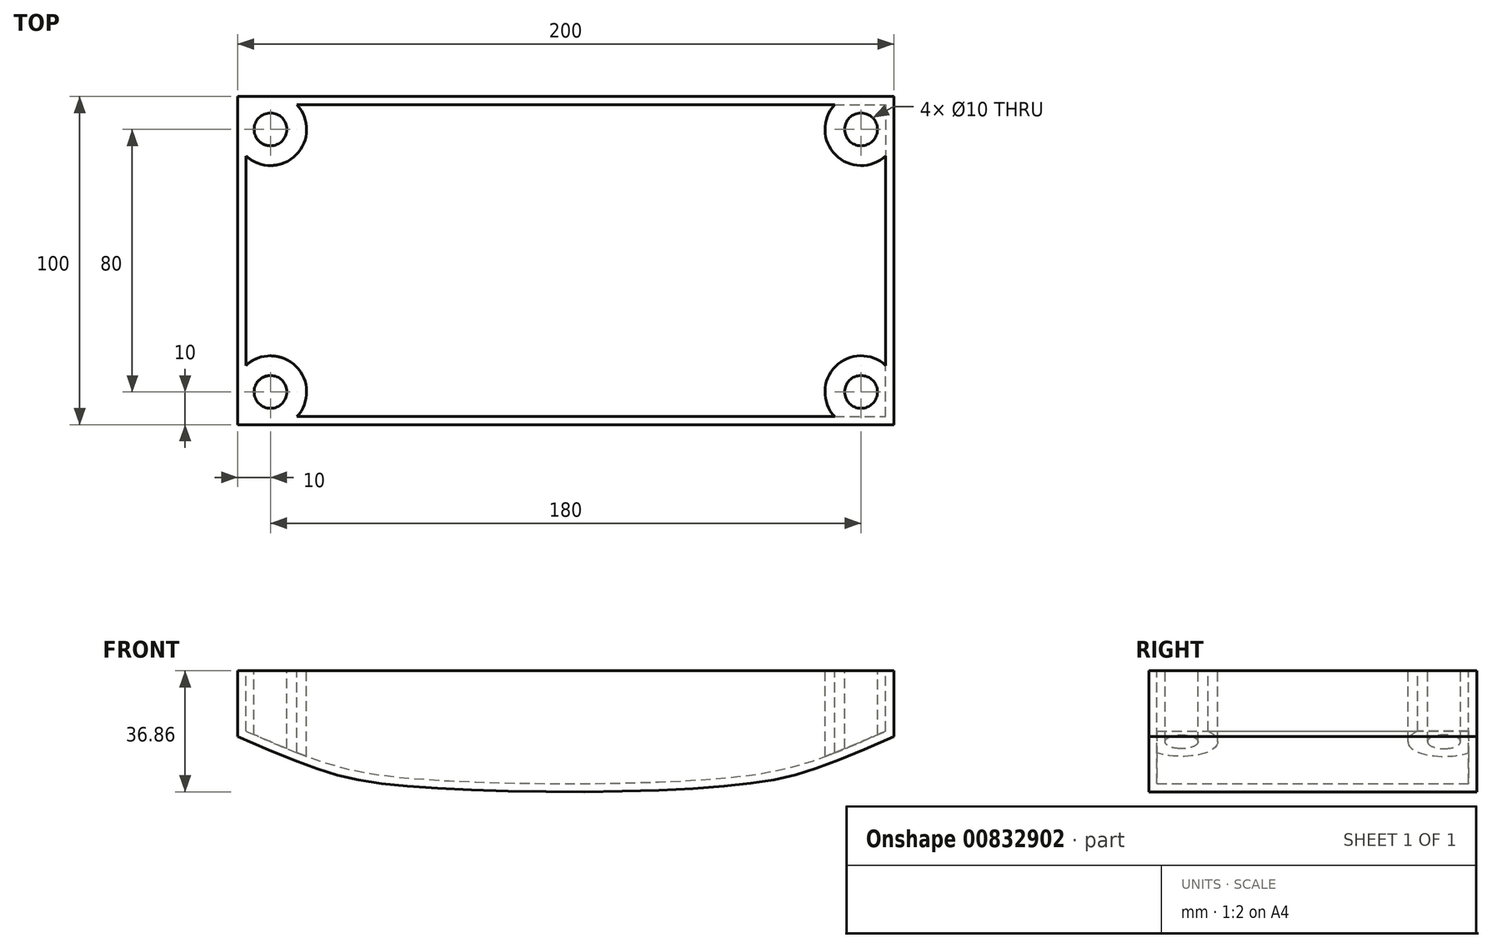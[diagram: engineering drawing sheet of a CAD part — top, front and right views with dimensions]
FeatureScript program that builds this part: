
annotation { "Feature Type Name" : "Feature", "Feature Type Description" : "" }
export const myFeature = defineFeature(function(context is Context, id is Id, definition is map)
    precondition{}
    {
        {
            var Q0;
            Q0=qCreatedBy(makeId("Front.planeOp"),FACE);
            var sketch = newSketch(context, id + "F0", { "sketchPlane" : qUnion([Q0])});
            skLineSegment(sketch, "E0.bottom", {"start": v(-100, 20) * mm, "end": v(100, 20) * mm});
            skLineSegment(sketch, "E0.left", {"start": v(-100, 20) * mm, "end": v(-100, 0) * mm});
            skLineSegment(sketch, "E0.right", {"start": v(100, 20) * mm, "end": v(100, 0) * mm});
            skFitSpline(sketch, "E1", {"points": [v(-100, 0) * mm, v(-50, -15) * mm, v(50, -15) * mm, v(100, 0) * mm], "startDerivative": vector(237.19, -104) * mm, "endDerivative": vector(226.22, 101.3) * mm});
            skPoint(sketch, "E2.orphan", {"position": v(100, -20) * mm});
            skSolve(sketch);
        }
        {
            var Q0;
            Q0=makeQuery(id+"F0.imprint","IMPRINT",FACE,{"disambiguationData":[TD([[makeQuery(id+"F0.imprint","IMPRINT",EDGE,{"derivedFrom":sQuery(id+"F0.wireOp",EDGE,"E0.bottom")}),-1.0]])]});
            extrude(context, id + "F1", {"entities" : qUnion([Q0]), "endBound" : BoundingType.SYMMETRIC, "depth" : 100 * mm, "offsetDistance" : 25 * mm});
        }
        {
            var Q0;
            Q0=makeQuery(id+"F1.opExtrude","SWEPT_FACE",FACE,{"disambiguationData":[OSD([sQuery(id+"F0.wireOp",EDGE,"E0.bottom")])]});
            shell(context, id + "F2", {"entities" : qUnion([Q0]), "thickness" : 2.5 * mm});
        }
        {
            var Q0;
            Q0=makeQuery(id+"F1.opExtrude","SWEPT_FACE",FACE,{"disambiguationData":[OSD([sQuery(id+"F0.wireOp",EDGE,"E0.bottom")])]});
            var sketch = newSketch(context, id + "F3", { "sketchPlane" : qUnion([Q0])});
            skCircle(sketch, "E3", {"center": v(-90, -40) * mm, "radius": 5 * mm});
            skCircle(sketch, "E4", {"center": v(-90, -40) * mm, "radius": 11 * mm});
            skSolve(sketch);
        }
        {
            var Q0;
            Q0=makeQuery(id+"F3.imprint","IMPRINT",FACE,{"disambiguationData":[TD([[makeQuery(id+"F3.imprint","IMPRINT",EDGE,{"derivedFrom":sQuery(id+"F3.wireOp",EDGE,"E3")}),-1.0]])]});
            extrude(context, id + "F4", {"entities" : qUnion([Q0]), "endBound" : BoundingType.UP_TO_NEXT, "oppositeDirection" : true, "depth" : 25 * mm, "offsetDistance" : 25 * mm});
        }
        {
            var Q0;
            Q0=makeQuery(id+"F4.opExtrude","SWEPT_BODY",BODY,{"disambiguationData":[OSD([sQuery(id+"F0.wireOp",EDGE,"E0.bottom"),sQuery(id+"F0.wireOp",EDGE,"E0.left"),sQuery(id+"F3.wireOp",EDGE,"E3"),sQuery(id+"F3.wireOp",EDGE,"E4")])]});
            var Q1;
            Q1=qCreatedBy(makeId("Front.planeOp"),FACE);
            mirror(context, id + "F5", {"entities" : qUnion([Q0]), "mirrorPlane" : qUnion([Q1])});
        }
        {
            var Q0;
            Q0=makeQuery(id+"F4.opExtrude","SWEPT_BODY",BODY,{"disambiguationData":[OSD([sQuery(id+"F0.wireOp",EDGE,"E0.bottom"),sQuery(id+"F0.wireOp",EDGE,"E0.left"),sQuery(id+"F3.wireOp",EDGE,"E3"),sQuery(id+"F3.wireOp",EDGE,"E4")])]});
            var Q1;
            Q1=makeQuery(id+"F5.opPattern","COPY",BODY,{"derivedFrom":makeQuery(id+"F4.opExtrude","SWEPT_BODY",BODY,{"disambiguationData":[OSD([sQuery(id+"F0.wireOp",EDGE,"E0.bottom"),sQuery(id+"F0.wireOp",EDGE,"E0.left"),sQuery(id+"F3.wireOp",EDGE,"E3"),sQuery(id+"F3.wireOp",EDGE,"E4")])]}),"instanceName":"1"});
            var Q2;
            Q2=qCreatedBy(makeId("Right.planeOp"),FACE);
            mirror(context, id + "F6", {"operationType" : NewBodyOperationType.ADD, "entities" : qUnion([Q0, Q1]), "mirrorPlane" : qUnion([Q2])});
        }
    });
